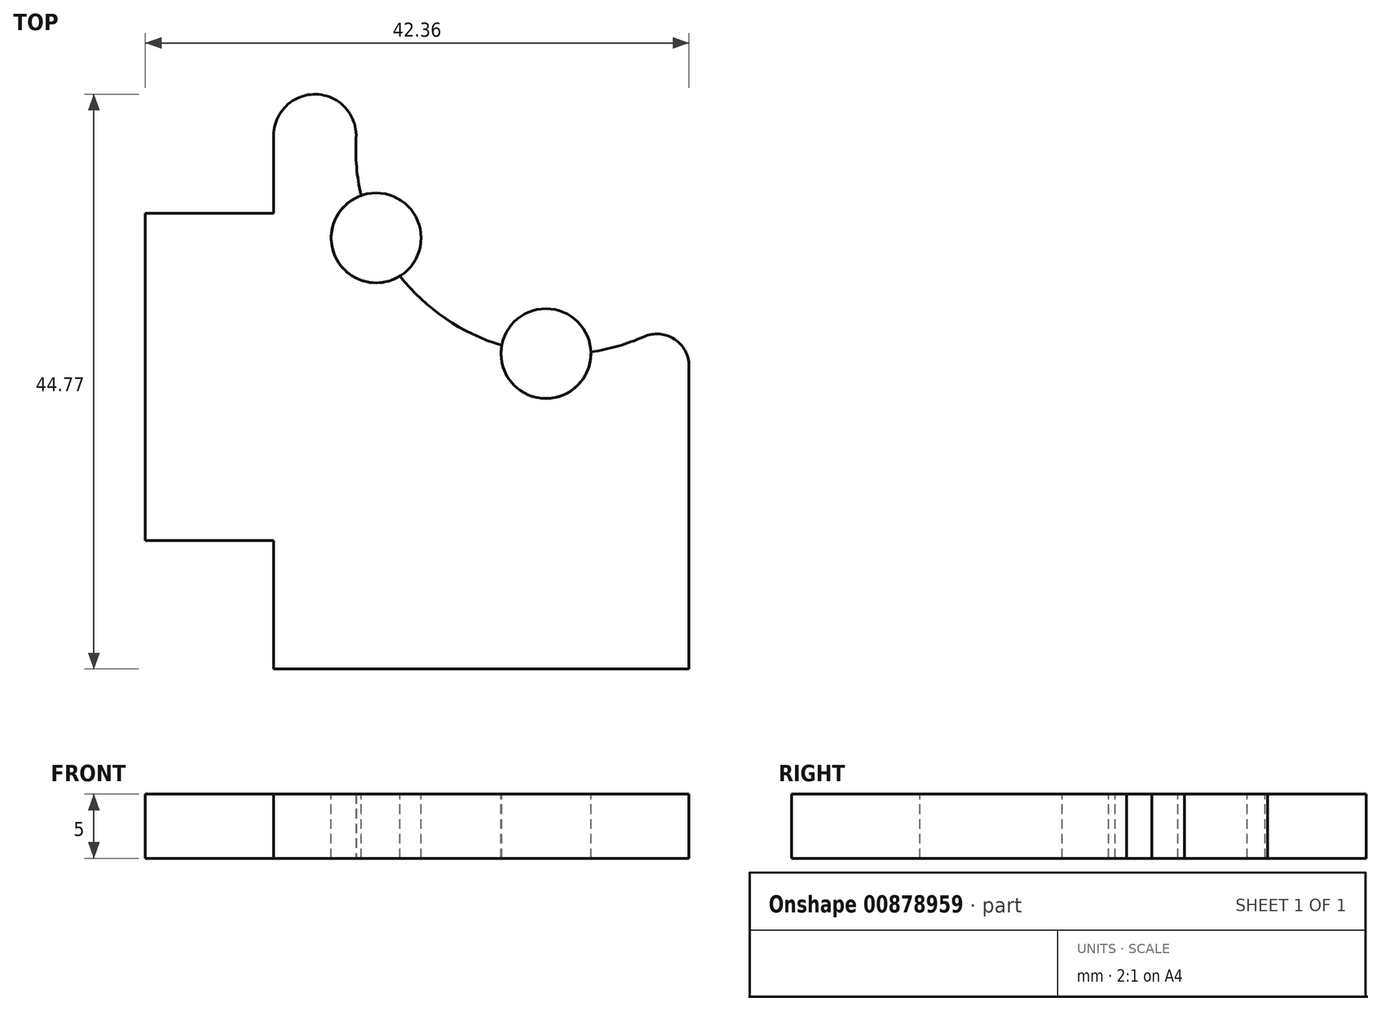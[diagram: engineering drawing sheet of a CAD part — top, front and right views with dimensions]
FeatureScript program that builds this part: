
annotation { "Feature Type Name" : "Feature", "Feature Type Description" : "" }
export const myFeature = defineFeature(function(context is Context, id is Id, definition is map)
    precondition{}
    {
        {
            var Q0;
            Q0=qCreatedBy(makeId("Top.planeOp"),FACE);
            var sketch = newSketch(context, id + "F0", { "sketchPlane" : qUnion([Q0])});
            skLineSegment(sketch, "E0.bottom", {"start": v(0, 0) * mm, "end": v(32.36, 0) * mm});
            skLineSegment(sketch, "E0.left", {"start": v(0, 0) * mm, "end": v(0, 31.55) * mm});
            skLineSegment(sketch, "E0.right", {"start": v(32.36, 0) * mm, "end": v(32.36, 13.6) * mm});
            skArc(sketch, "E1", {"start": v(6.42, 31.38) * mm, "mid": v(13.3, 17.36) * mm, "end": v(28.85, 15.88) * mm});
            skCircle(sketch, "E2", {"center": v(29.86, 13.6) * mm, "radius": 2.5 * mm});
            skCircle(sketch, "E3", {"center": v(3.21, 31.55) * mm, "radius": 3.21 * mm});
            skSolve(sketch);
        }
        {
            var Q0;
            Q0=qSketchRegion(id+"F0",true);
            extrude(context, id + "F1", {"entities" : qUnion([Q0]), "depth" : 5 * mm, "offsetDistance" : 25 * mm});
        }
        {
            var Q0;
            Q0=makeQuery(id+"F1.opExtrude","CAP_FACE",FACE,{"disambiguationData":[OSD([sQuery(id+"F0.wireOp",EDGE,"E0.bottom"),sQuery(id+"F0.wireOp",EDGE,"E0.left"),sQuery(id+"F0.wireOp",EDGE,"E0.right"),sQuery(id+"F0.wireOp",EDGE,"E1"),sQuery(id+"F0.wireOp",EDGE,"E2"),sQuery(id+"F0.wireOp",EDGE,"E3")])],"isStart":false});
            var sketch = newSketch(context, id + "F2", { "sketchPlane" : qUnion([Q0])});
            skLineSegment(sketch, "E4", {"start": v(32.36, 0) * mm, "end": v(32.36, -10) * mm});
            skLineSegment(sketch, "E5", {"start": v(32.36, -10) * mm, "end": v(0, -10) * mm});
            skLineSegment(sketch, "E6", {"start": v(0, -10) * mm, "end": v(0, 0) * mm});
            skLineSegment(sketch, "E7", {"start": v(0, 0) * mm, "end": v(-10, 0) * mm});
            skLineSegment(sketch, "E8", {"start": v(-10, 0) * mm, "end": v(-10, 25.49) * mm});
            skLineSegment(sketch, "E9", {"start": v(-10, 25.49) * mm, "end": v(0, 25.49) * mm});
            skLineSegment(sketch, "E10", {"start": v(0, 25.49) * mm, "end": v(-110.38, 52.94) * mm});
            skSolve(sketch);
        }
        {
            var Q0;
            {var subQ0=makeQuery(id+"F1.opExtrude","CAP_EDGE",EDGE,{"disambiguationData":[OSD([sQuery(id+"F0.wireOp",EDGE,"E0.bottom")])],"isStart":false});Q0=makeQuery(id+"F2.imprint","IMPRINT",FACE,{"disambiguationData":[TD([[makeQuery(id+"F2.imprint","IMPRINT",EDGE,{"derivedFrom":subQ0}),1.0]])]});}
            var Q1;
            Q1=makeQuery(id+"F2.imprint","IMPRINT",FACE,{"disambiguationData":[TD([[makeQuery(id+"F2.imprint","IMPRINT",EDGE,{"derivedFrom":sQuery(id+"F2.wireOp",EDGE,"E4")}),-1.0]])]});
            var Q2;
            {var subQ0=sQuery(id+"F2.wireOp",EDGE,"E7");Q2=makeQuery(id+"F2.imprint","IMPRINT",FACE,{"disambiguationData":[TD([[makeQuery(id+"F2.imprint","IMPRINT",EDGE,{"derivedFrom":subQ0}),-1.0]])]});}
            extrude(context, id + "F3", {"entities" : qUnion([Q0, Q1, Q2]), "operationType" : NewBodyOperationType.ADD, "oppositeDirection" : true, "depth" : 5 * mm, "offsetDistance" : 25 * mm});
        }
        {
            var Q0;
            {var subQ0=sQuery(id+"F0.wireOp",EDGE,"E3");var subQ1=sQuery(id+"F0.wireOp",EDGE,"E2");var subQ2=sQuery(id+"F0.wireOp",EDGE,"E1");var subQ3=sQuery(id+"F0.wireOp",EDGE,"E0.right");var subQ4=sQuery(id+"F0.wireOp",EDGE,"E0.left");Q0=makeQuery(id+"F3.boolean.opBoolean","MERGE",FACE,{"derivedFrom":[makeQuery(id+"F1.opExtrude","CAP_FACE",FACE,{"disambiguationData":[OSD([sQuery(id+"F0.wireOp",EDGE,"E0.bottom"),subQ4,subQ3,subQ2,subQ1,subQ0])],"isStart":false}),makeQuery(id+"F3.opExtrude","CAP_FACE",FACE,{"disambiguationData":[OSD([subQ4,subQ3,subQ2,subQ1,subQ0,sQuery(id+"F2.wireOp",EDGE,"E4"),sQuery(id+"F2.wireOp",EDGE,"E5"),sQuery(id+"F2.wireOp",EDGE,"E6"),sQuery(id+"F2.wireOp",EDGE,"E7"),sQuery(id+"F2.wireOp",EDGE,"E8"),sQuery(id+"F2.wireOp",EDGE,"E9")])],"isStart":true})]});}
            var sketch = newSketch(context, id + "F4", { "sketchPlane" : qUnion([Q0])});
            skCircle(sketch, "E11", {"center": v(7.99, 23.58) * mm, "radius": 3.5 * mm});
            skCircle(sketch, "E12", {"center": v(21.22, 14.57) * mm, "radius": 3.5 * mm});
            skSolve(sketch);
        }
        {
            var Q0;
            Q0 = qSketchRegion(id + "F4", true);
            extrude(context, id + "F5", {"entities" : qUnion([Q0]), "operationType" : NewBodyOperationType.REMOVE, "oppositeDirection" : true, "depth" : 5 * mm, "offsetDistance" : 25 * mm});
        }
        {
            var Q0;
            Q0 = qSketchRegion(id + "F4", true);
            extrude(context, id + "F6", {"entities" : qUnion([Q0]), "oppositeDirection" : true, "depth" : 5 * mm, "offsetDistance" : 25 * mm});
        }
    });
